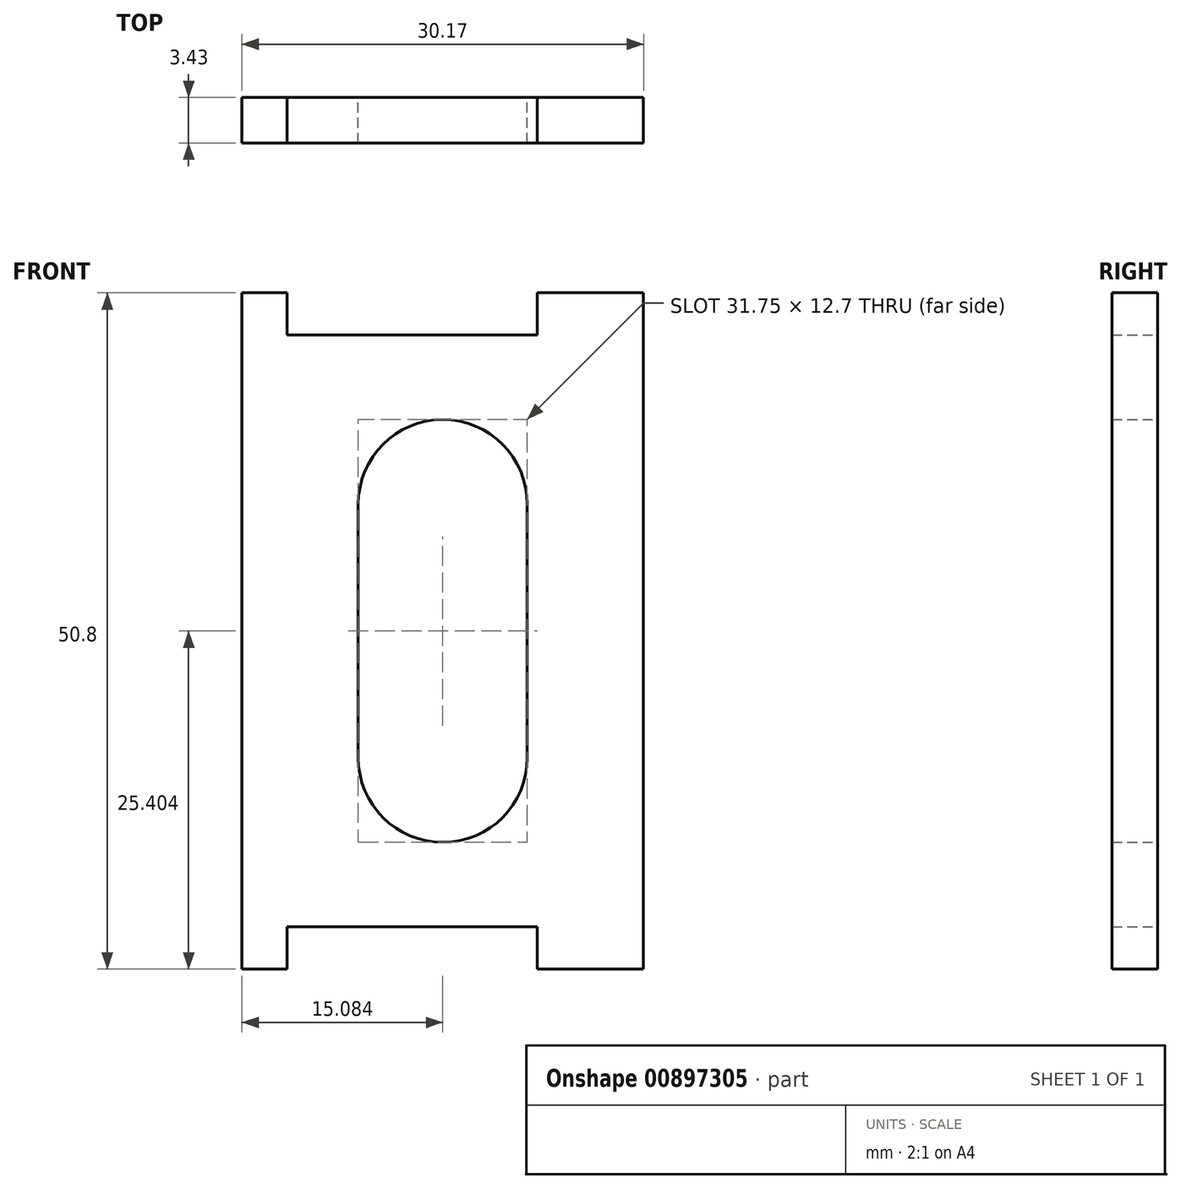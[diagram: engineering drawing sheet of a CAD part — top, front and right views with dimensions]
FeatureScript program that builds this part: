
annotation { "Feature Type Name" : "Feature", "Feature Type Description" : "" }
export const myFeature = defineFeature(function(context is Context, id is Id, definition is map)
    precondition{}
    {
        {
            var Q0;
            Q0=qCreatedBy(makeId("Front.planeOp"),FACE);
            var sketch = newSketch(context, id + "F0", { "sketchPlane" : qUnion([Q0])});
            skLineSegment(sketch, "E0", {"start": v(497.05, 17.61) * mm, "end": v(497.05, 68.41) * mm});
            skLineSegment(sketch, "E1", {"start": v(489.08, 17.61) * mm, "end": v(497.05, 17.61) * mm});
            skLineSegment(sketch, "E2", {"start": v(489.08, 20.79) * mm, "end": v(489.08, 17.61) * mm});
            skLineSegment(sketch, "E3", {"start": v(466.88, 68.41) * mm, "end": v(466.88, 17.61) * mm});
            skLineSegment(sketch, "E4", {"start": v(489.08, 68.41) * mm, "end": v(489.08, 65.24) * mm});
            skLineSegment(sketch, "E5", {"start": v(497.05, 68.41) * mm, "end": v(489.08, 68.41) * mm});
            skArc(sketch, "E6", {"start": v(475.61, 33.49) * mm, "mid": v(481.96, 27.14) * mm, "end": v(488.31, 33.49) * mm});
            skLineSegment(sketch, "E7", {"start": v(488.31, 33.49) * mm, "end": v(488.31, 52.54) * mm});
            skLineSegment(sketch, "E8", {"start": v(470.28, 17.61) * mm, "end": v(470.28, 20.79) * mm});
            skLineSegment(sketch, "E9", {"start": v(466.88, 17.61) * mm, "end": v(470.28, 17.61) * mm});
            skLineSegment(sketch, "E10", {"start": v(475.61, 52.54) * mm, "end": v(475.61, 33.49) * mm});
            skLineSegment(sketch, "E11", {"start": v(470.28, 20.79) * mm, "end": v(489.08, 20.79) * mm});
            skLineSegment(sketch, "E12", {"start": v(470.28, 65.24) * mm, "end": v(470.28, 68.41) * mm});
            skLineSegment(sketch, "E13", {"start": v(489.08, 65.24) * mm, "end": v(470.28, 65.24) * mm});
            skArc(sketch, "E14", {"start": v(488.31, 52.54) * mm, "mid": v(481.96, 58.89) * mm, "end": v(475.61, 52.54) * mm});
            skLineSegment(sketch, "E15", {"start": v(470.28, 68.41) * mm, "end": v(466.88, 68.41) * mm});
            skSolve(sketch);
        }
        {
            var Q0;
            Q0 = qSketchRegion(id + "F0", true);
            extrude(context, id + "F1", {"entities" : qUnion([Q0]), "depth" : 3.43 * mm, "offsetDistance" : 25.4 * mm});
        }
    });
